# Revit family: LAMP_HANCE DOWNLIGHT SEMIRECESSED SPOT 1000_2000
name_source: partatom
category: Modelos genéricos
revit_build: Autodesk Revit 2015 (Build: 20140606_1530(x64)
units: mm (PartAtom-declared; Revit-internal decimal feet)

## types (8) — shared parameters
Aro 1000/2000 = Sí
Aro 3000/4000 = No
CRI = 80
Comentarios de tipo = Availability of tilting between 0º and 85º when placed in a project.
Diameter = 143 mm
Elevación por defecto = 1219 mm
Fabricante = LAMP
Gear = Electronic
Installation instructions = https://www.lamp.es
Insulation class = II
Lamp = COB LED
Last update = 22/11/2019
Luminaire type = Indoor - Recessed downlight
MacAdam = 3
Manufacturer URL = http://www.lamp.es
Manufacturer country = Spain
Manufacturer name = LAMP
Material interior aro = LAMP_Aluminio Hance Negro
Model explanation = Availability of tilting between 0º and 85º when placed in a project.
Power Supply = 220-240V 50/60Hz
Product URL = https://www.lamp.es
Product datasheet = http://www.lamp.es
Protection rating = IP20
Radio aro exterior = 36 mm
Recessed diameter = 132 mm  [stored 0.433071 ft]
Type = COB PHILIPS
Weight = 0.79 kg

## per-type parameters (varying)
| type | Descripción | Efficacy | Finish | IEE | Initial color | Initial intensity | LED Lifetime | Material aro | Modelo | Photometric web file | Plum | Power | Product code |
| 710LM 4000K 1000 BLACK | HANCE DOWN SEMIREC 1000 NW SP BK. | 93 lm/W | Texturised white RAL 9010 | A+ | 4000 K | 710 lm | 50.000 L90 B10 | LAMP_Aluminio Hance Negro | HD1SR10SP840NBB | Cuerpo Hance BASE (tilting)_SP : 710LM 4000K 1000 BLACK | 8 W | 7 W | HD1SR10SP840NBB |
| 710LM 4000K 1000 WHITE | HANCE DOWN SEMIREC 1000 NW SP WH. | 93 lm/W | Texturised black RAL 9011 | A+ | 4000 K | 710 lm | 50.000 L90 B10 | LAMP_Aluminio Hance Blanco | HD1SR10SP840NBW | Cuerpo Hance BASE (tilting)_SP : 710LM 4000K 1000 WHITE | 8 W | 7 W | HD1SR10SP840NBW |
| 773LM 3000K 1000 BLACK | HANCE DOWN SEMIREC 1000 WW SP BK. | 100 lm/W | Texturised white RAL 9010 | A+ | 3000 K | 773 lm | 50.000 L90 B10 | LAMP_Aluminio Hance Negro | HD1SR10SP830NBB | Cuerpo Hance BASE (tilting)_SP : 773LM 3000K 1000 BLACK | 8 W | 7 W | HD1SR10SP830NBB |
| 773LM 3000K 1000 WHITE | HANCE DOWN SEMIREC 1000 WW SP WH. | 100 lm/W | Texturised black RAL 9011 | A+ | 3000 K | 773 lm | 50.000 L90 B10 | LAMP_Aluminio Hance Blanco | HD1SR10SP830NBW | Cuerpo Hance BASE (tilting)_SP : 773LM 3000K 1000 WHITE | 8 W | 7 W | HD1SR10SP830NBW |
| 1644LM 4000K 2000 BLACK | HANCE DOWN SEMIREC 2000 NW SP BK. | 80 lm/W | Texturised black RAL 9011 | A+ | 4000 K | 1644 lm | 50.000 L80 B10 | LAMP_Aluminio Hance Negro | HD1SR20SP840NBB | Cuerpo Hance BASE (tilting)_SP : 1644LM 4000K 2000 BLACK | 21 W | 18 W | HD1SR20SP840NBB |
| 1644LM 4000K 2000 WHITE | HANCE DOWN SEMIREC 2000 NW SP WH. | 80 lm/W | Texturised white RAL 9010 | A+ | 4000 K | 1644 lm | 50.000 L80 B10 | LAMP_Aluminio Hance Blanco | HD1SR20SP840NBW | Cuerpo Hance BASE (tilting)_SP : 1644LM 4000K 2000 WHITE | 21 W | 18 W | HD1SR20SP840NBW |
| 1707LM 3000K 2000 BLACK | HANCE DOWN SEMIREC 2000 WW SP BK. | 82 lm/W | Texturised black RAL 9011 | A | 3000 K | 1707 lm | 50.000 L80 B10 | LAMP_Aluminio Hance Negro | HD1SR20SP830NBB | Cuerpo Hance BASE (tilting)_SP : 1707LM 3000K 2000 BLACK | 21 W | 18 W | HD1SR20SP830NBB |
| 1707LM 3000K 2000 WHITE | HANCE DOWN SEMIREC 2000 WW SP WH. | 82 lm/W | Texturised white RAL 9010 | A | 3000 K | 1707 lm | 50.000 L80 B10 | LAMP_Aluminio Hance Blanco | HD1SR20SP830NBW | Cuerpo Hance BASE (tilting)_SP : 1707LM 3000K 2000 WHITE | 21 W | 18 W | HD1SR20SP830NBW |

note: [stored X ft] marks values corroborated as IEEE doubles in the binary element streams (Revit-internal decimal feet)
